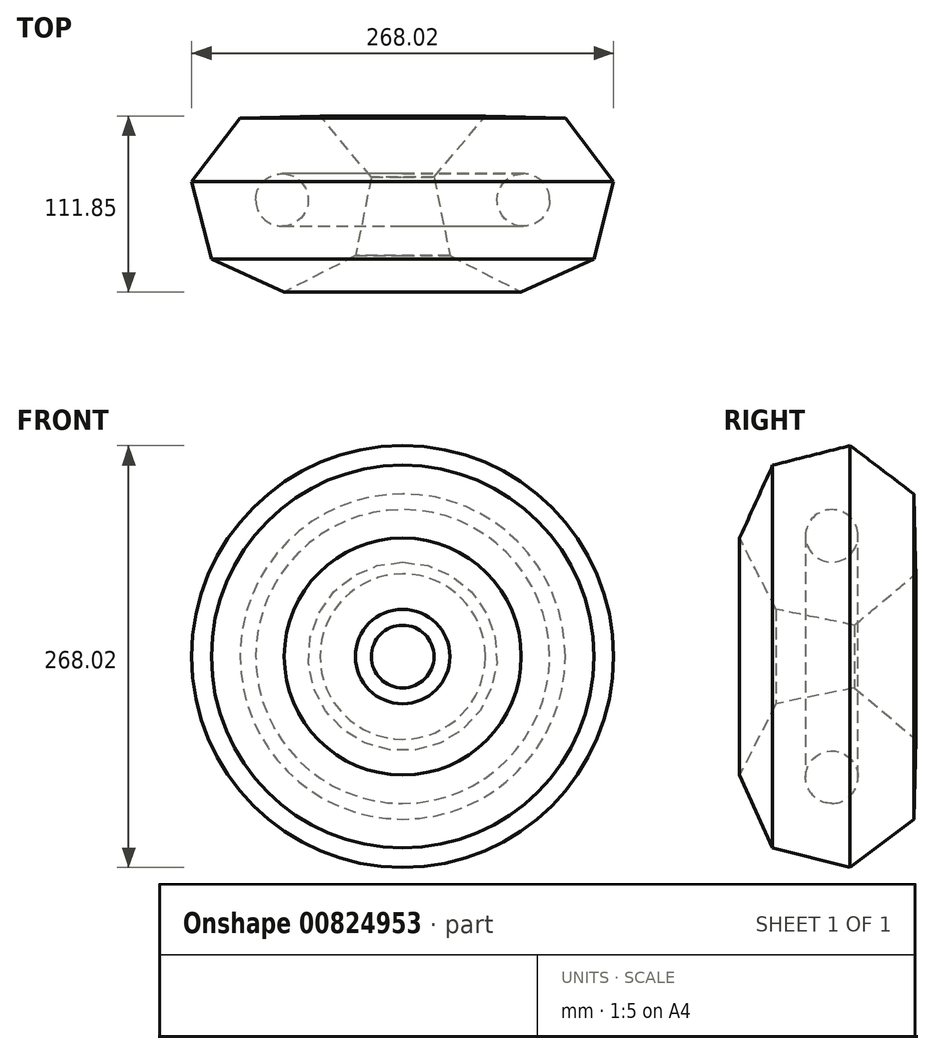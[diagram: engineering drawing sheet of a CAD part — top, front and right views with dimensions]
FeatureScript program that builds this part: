
annotation { "Feature Type Name" : "Feature", "Feature Type Description" : "" }
export const myFeature = defineFeature(function(context is Context, id is Id, definition is map)
    precondition{}
    {
        {
            var Q0;
            Q0=qCreatedBy(makeId("Top.planeOp"),FACE);
            var sketch = newSketch(context, id + "F0", { "sketchPlane" : qUnion([Q0])});
            skCircle(sketch, "E0.cCircle", {"center": v(0, 0) * mm, "radius": 52.74 * mm, "construction": true});
            skLineSegment(sketch, "E0.0", {"start": v(56.75, 14.37) * mm, "end": v(46.62, -35.4) * mm});
            skLineSegment(sketch, "E0.1", {"start": v(46.62, -35.4) * mm, "end": v(1.39, -58.52) * mm});
            skLineSegment(sketch, "E0.2", {"start": v(1.39, -58.52) * mm, "end": v(-44.9, -37.57) * mm});
            skLineSegment(sketch, "E0.3", {"start": v(-44.9, -37.57) * mm, "end": v(-57.37, 11.67) * mm});
            skLineSegment(sketch, "E0.4", {"start": v(-57.37, 11.67) * mm, "end": v(-26.64, 52.13) * mm});
            skLineSegment(sketch, "E0.5", {"start": v(-26.64, 52.13) * mm, "end": v(24.14, 53.33) * mm});
            skLineSegment(sketch, "E0.6", {"start": v(24.14, 53.33) * mm, "end": v(56.75, 14.37) * mm});
            skPoint(sketch, "E0.0.midPoint", {"position": v(51.68, -10.52) * mm});
            skCircle(sketch, "E1", {"center": v(0, 0) * mm, "radius": 16.68 * mm});
            skSolve(sketch);
        }
        {
            var Q0;
            Q0=qCreatedBy(makeId("Top.planeOp"),FACE);
            var sketch = newSketch(context, id + "F1", { "sketchPlane" : qUnion([Q0])});
            skLineSegment(sketch, "E2", {"start": v(76.64, 70.57) * mm, "end": v(76.64, -64.3) * mm, "construction": true});
            skSolve(sketch);
        }
        {
            var Q0;
            Q0=makeQuery(id+"F0.imprint","IMPRINT",FACE,{"disambiguationData":[TD([[makeQuery(id+"F0.imprint","IMPRINT",EDGE,{"derivedFrom":sQuery(id+"F0.wireOp",EDGE,"E0.0")}),-1.0]])]});
            var Q1;
            Q1=sQuery(id+"F1.wireOp",EDGE,"E2");
            revolve(context, id + "F2", {"surfaceOperationType" : NewSurfaceOperationType.NEW, "entities" : qUnion([Q0]), "axis" : qUnion([Q1]), "revolveType" : RevolveType.FULL});
        }
    });
